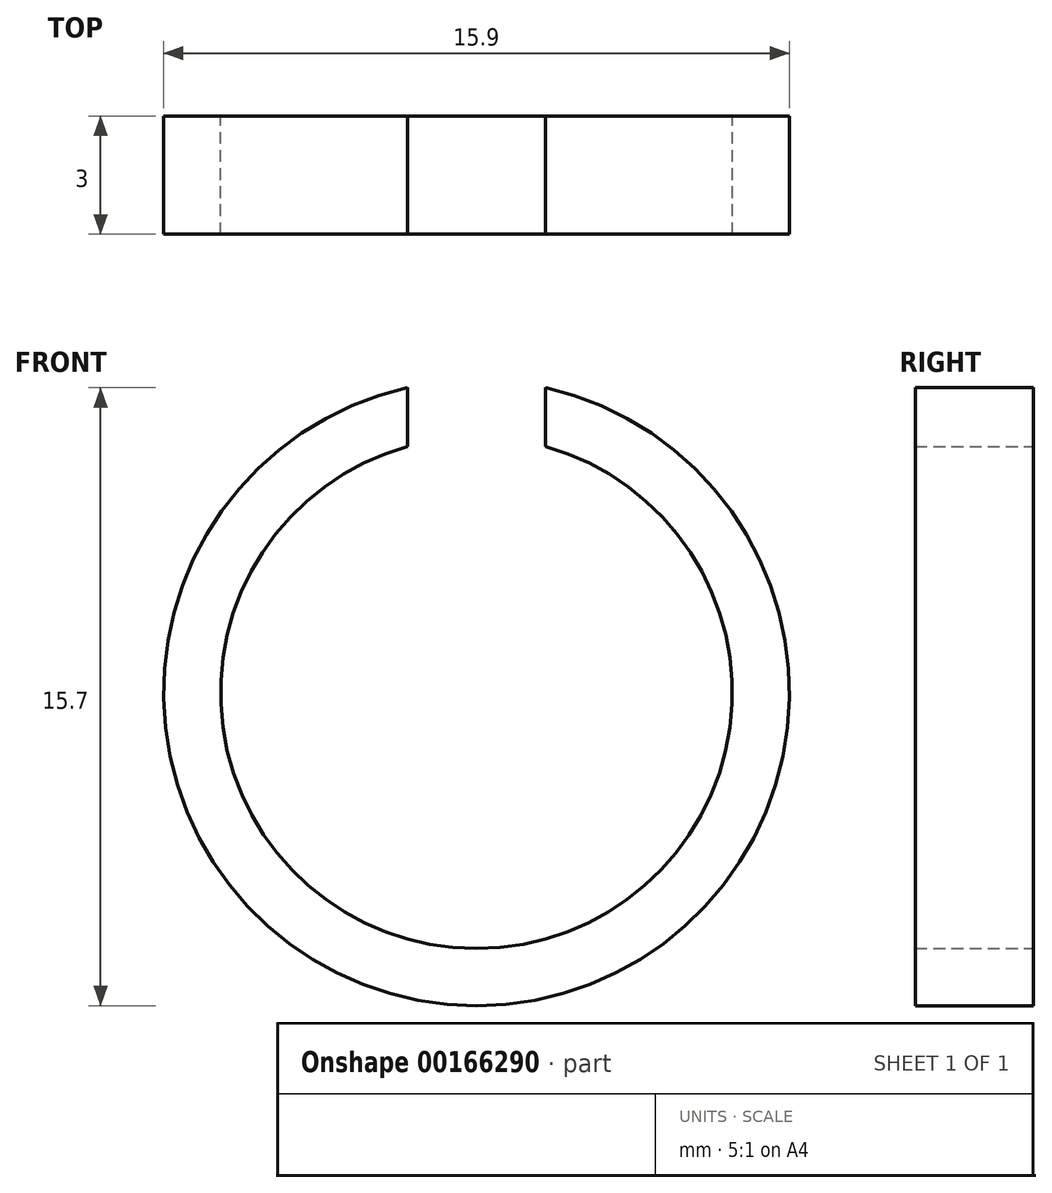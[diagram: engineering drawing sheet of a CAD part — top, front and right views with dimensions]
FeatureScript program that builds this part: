
annotation { "Feature Type Name" : "Feature", "Feature Type Description" : "" }
export const myFeature = defineFeature(function(context is Context, id is Id, definition is map)
    precondition{}
    {
        {
            assignVariable(context, id + "F0", {"name" : "Main_Length", "anyValue" : 3});
        }
        {
            var Q0;
            Q0=qCreatedBy(makeId("Front.planeOp"),FACE);
            var sketch = newSketch(context, id + "F1", { "sketchPlane" : qUnion([Q0])});
            skCircle(sketch, "E0", {"center": v(0, 0) * mm, "radius": 7.95 * mm});
            skCircle(sketch, "E1", {"center": v(0, 0) * mm, "radius": 6.5 * mm});
            skSolve(sketch);
        }
        {
            var Q0;
            Q0=makeQuery(id+"F1.imprint","IMPRINT",FACE,{"disambiguationData":[TD([[makeQuery(id+"F1.imprint","IMPRINT",EDGE,{"derivedFrom":sQuery(id+"F1.wireOp",EDGE,"E0")}),1.0]])]});
            extrude(context, id + "F2", {"entities" : qUnion([Q0]), "depth" : (getVariable(context, 'Main_Length')) * mm});
        }
        {
            var Q0;
            Q0=qCreatedBy(makeId("Top.planeOp"),FACE);
            var sketch = newSketch(context, id + "F3", { "sketchPlane" : qUnion([Q0])});
            skLineSegment(sketch, "E2", {"start": v(-1.75, 0) * mm, "end": v(-1.75, -3) * mm});
            skLineSegment(sketch, "E3", {"start": v(1.75, 0) * mm, "end": v(1.75, -3) * mm});
            skLineSegment(sketch, "E4.0", {"start": v(7.95, -3) * mm, "end": v(-7.95, -3) * mm});
            skLineSegment(sketch, "E5", {"start": v(-1.75, 0) * mm, "end": v(1.75, 0) * mm});
            skLineSegment(sketch, "E6.0", {"start": v(7.95, 0) * mm, "end": v(-7.95, 0) * mm});
            skSolve(sketch);
        }
        {
            var Q0;
            {var subQ0=sQuery(id+"F3.wireOp",EDGE,"E2");Q0=makeQuery(id+"F3.imprint","IMPRINT",FACE,{"disambiguationData":[TD([[makeQuery(id+"F3.imprint","IMPRINT",EDGE,{"derivedFrom":subQ0}),1.0]])]});}
            extrude(context, id + "F4", {"entities" : qUnion([Q0]), "operationType" : NewBodyOperationType.REMOVE, "endBound" : BoundingType.THROUGH_ALL, "depth" : 25 * mm});
        }
    });
